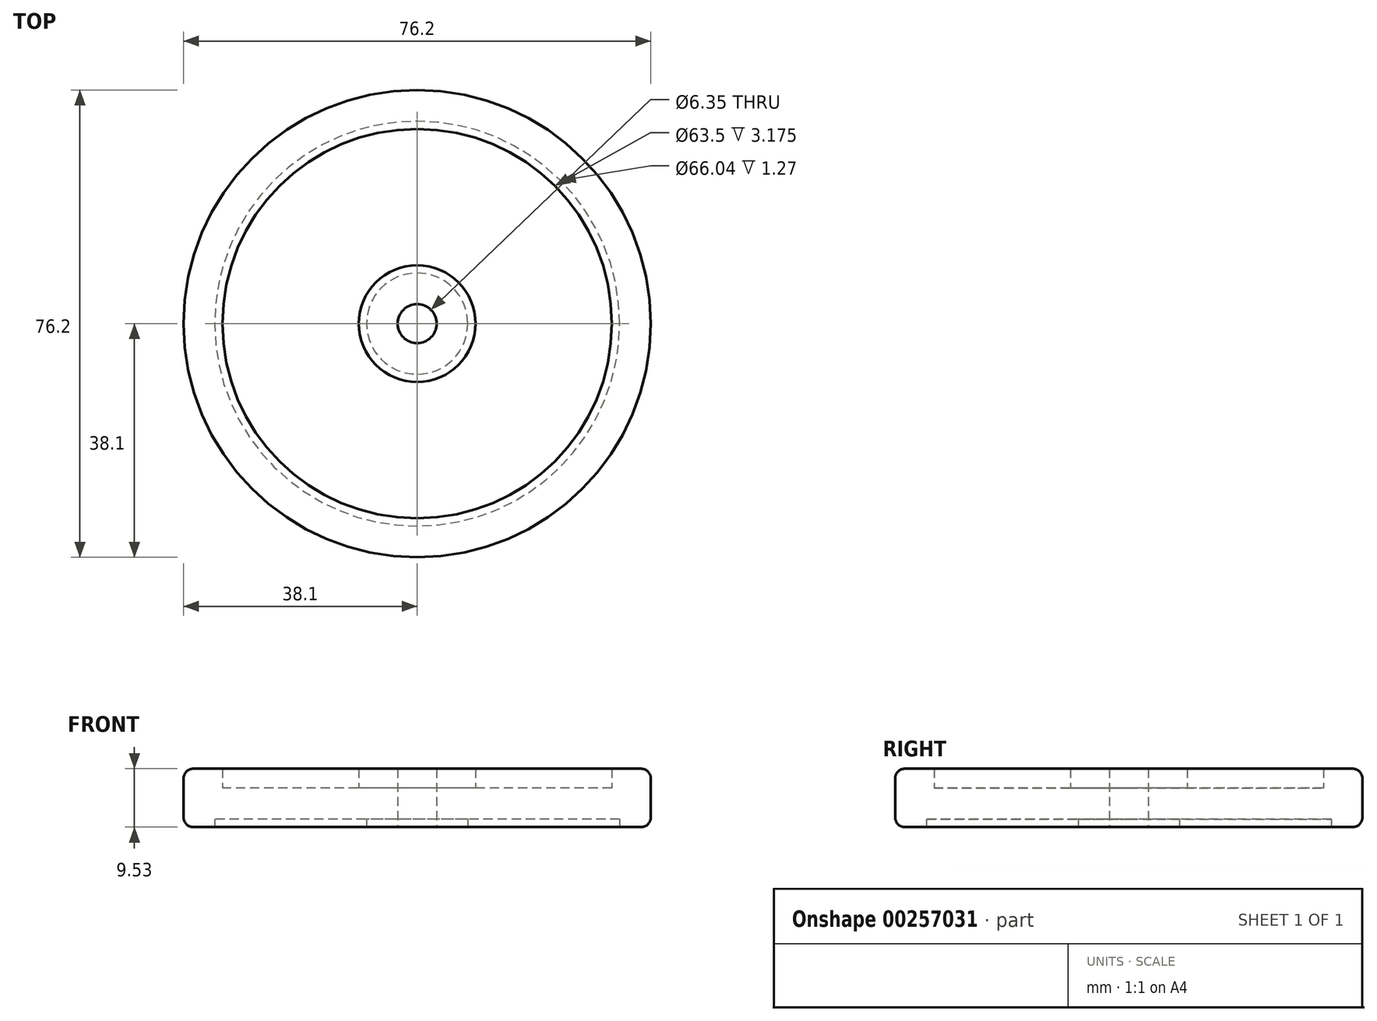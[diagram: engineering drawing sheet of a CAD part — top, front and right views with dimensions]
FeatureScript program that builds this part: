
annotation { "Feature Type Name" : "Feature", "Feature Type Description" : "" }
export const myFeature = defineFeature(function(context is Context, id is Id, definition is map)
    precondition{}
    {
        {
            var Q0;
            Q0=qCreatedBy(makeId("Top.planeOp"),FACE);
            var sketch = newSketch(context, id + "F0", { "sketchPlane" : qUnion([Q0])});
            skCircle(sketch, "E0", {"center": v(0, 0) * mm, "radius": 38.1 * mm});
            skCircle(sketch, "E1", {"center": v(0, 0) * mm, "radius": 3.18 * mm});
            skSolve(sketch);
        }
        {
            var Q0;
            Q0 = qSketchRegion(id + "F0", true);
            extrude(context, id + "F1", {"entities" : qUnion([Q0]), "depth" : 9.52 * mm});
        }
        {
            var Q0;
            Q0=makeQuery(id+"F1.opExtrude","CAP_EDGE",EDGE,{"disambiguationData":[OSD([sQuery(id+"F0.wireOp",EDGE,"E0")])],"isStart":false});
            var Q1;
            Q1=makeQuery(id+"F1.opExtrude","CAP_EDGE",EDGE,{"disambiguationData":[OSD([sQuery(id+"F0.wireOp",EDGE,"E0")])],"isStart":true});
            fillet(context, id + "F2", {"entities" : qUnion([Q0, Q1]), "radius" : 1.59 * mm, "tangentPropagation" : true, "allowEdgeOverflow" : false});
        }
        {
            var Q0;
            Q0=makeQuery(id+"F1.opExtrude","CAP_FACE",FACE,{"disambiguationData":[OSD([sQuery(id+"F0.wireOp",EDGE,"E0"),sQuery(id+"F0.wireOp",EDGE,"E1")])],"isStart":false});
            shell(context, id + "F3", {"entities" : qUnion([Q0]), "thickness" : 6.35 * mm});
        }
        {
            var Q0;
            Q0=makeQuery(id+"F1.opExtrude","CAP_FACE",FACE,{"disambiguationData":[OSD([sQuery(id+"F0.wireOp",EDGE,"E0"),sQuery(id+"F0.wireOp",EDGE,"E1")])],"isStart":true});
            shell(context, id + "F4", {"entities" : qUnion([Q0]), "thickness" : 5.08 * mm});
        }
    });
